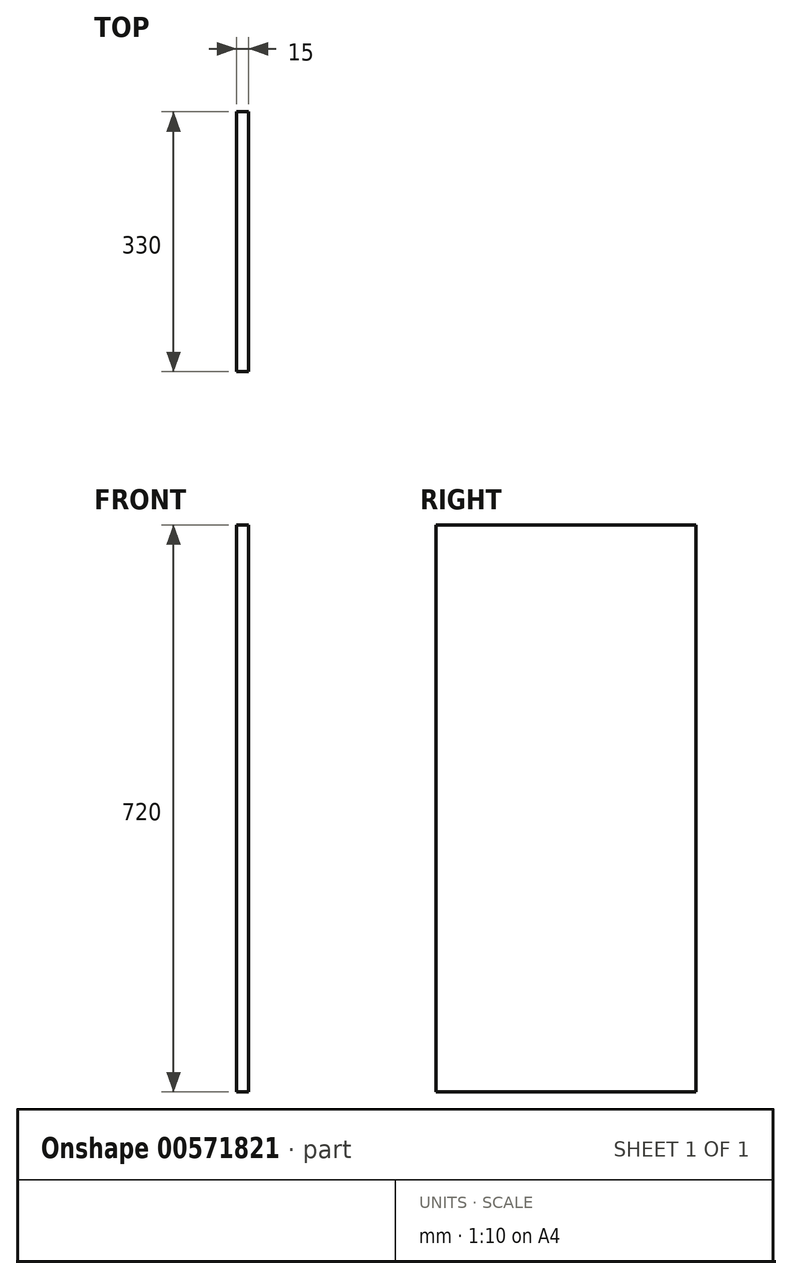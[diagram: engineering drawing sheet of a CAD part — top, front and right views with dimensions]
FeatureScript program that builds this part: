
annotation { "Feature Type Name" : "Feature", "Feature Type Description" : "" }
export const myFeature = defineFeature(function(context is Context, id is Id, definition is map)
    precondition{}
    {
        {
            var Q0;
            Q0=qCreatedBy(makeId("Front.planeOp"),FACE);
            var sketch = newSketch(context, id + "F0", { "sketchPlane" : qUnion([Q0])});
            skLineSegment(sketch, "E0.bottom", {"start": v(0, 0) * mm, "end": v(-15, 0) * mm});
            skLineSegment(sketch, "E0.top", {"start": v(0, 720) * mm, "end": v(-15, 720) * mm});
            skLineSegment(sketch, "E0.left", {"start": v(0, 0) * mm, "end": v(0, 720) * mm});
            skLineSegment(sketch, "E0.right", {"start": v(-15, 0) * mm, "end": v(-15, 720) * mm});
            skSolve(sketch);
        }
        {
            var Q0;
            Q0=makeQuery(id+"F0.imprint","IMPRINT",FACE,{"disambiguationData":[TD([[makeQuery(id+"F0.imprint","IMPRINT",EDGE,{"derivedFrom":sQuery(id+"F0.wireOp",EDGE,"E0.bottom")}),-1.0]])]});
            extrude(context, id + "F1", {"entities" : qUnion([Q0]), "oppositeDirection" : true, "depth" : 330 * mm, "offsetDistance" : 25 * mm});
        }
    });
